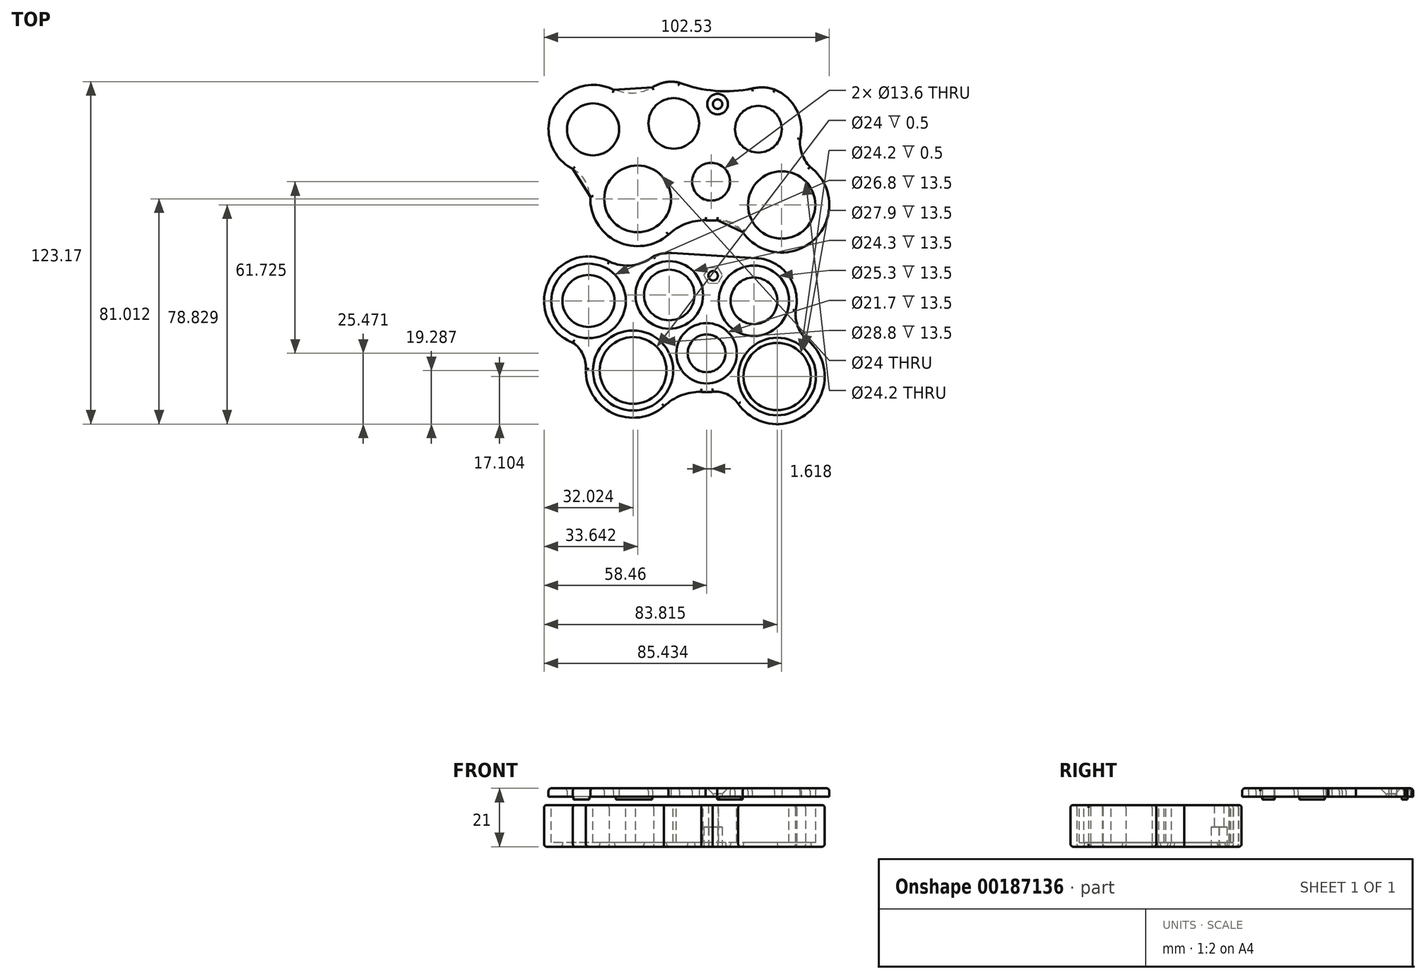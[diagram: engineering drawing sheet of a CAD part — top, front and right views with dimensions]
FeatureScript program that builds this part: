
annotation { "Feature Type Name" : "Feature", "Feature Type Description" : "" }
export const myFeature = defineFeature(function(context is Context, id is Id, definition is map)
    precondition{}
    {
        {
            var Q0;
            Q0=qCreatedBy(makeId("Top.planeOp"),FACE);
            var sketch = newSketch(context, id + "F0", { "sketchPlane" : qUnion([Q0])});
            skArc(sketch, "E0", {"start": v(-18.58, 19.68) * mm, "mid": v(-40.56, 11.98) * mm, "end": v(-31.57, -9.5) * mm});
            skArc(sketch, "E1", {"start": v(2.43, 22.7) * mm, "mid": v(-0.12, 22.37) * mm, "end": v(-2.57, 21.62) * mm});
            skArc(sketch, "E2", {"start": v(48.5, 2.02) * mm, "mid": v(45.84, 14.74) * mm, "end": v(34.4, 20.9) * mm});
            skArc(sketch, "E3", {"start": v(14.55, -27.21) * mm, "mid": v(16.64, -27.35) * mm, "end": v(18.72, -27.17) * mm});
            skArc(sketch, "E4", {"start": v(27.86, -31.53) * mm, "mid": v(53.8, -33.97) * mm, "end": v(52.05, -7.98) * mm});
            skArc(sketch, "E5", {"start": v(-26.9, -18.77) * mm, "mid": v(-17.33, -34.84) * mm, "end": v(1.21, -32.38) * mm});
            skCircle(sketch, "E6", {"center": v(-25.95, 5.48) * mm, "radius": 9.35 * mm});
            skCircle(sketch, "E7", {"center": v(-9.93, -19.53) * mm, "radius": 12 * mm});
            skCircle(sketch, "E8", {"center": v(3.07, 7.61) * mm, "radius": 9.1 * mm});
            skCircle(sketch, "E9", {"center": v(16.51, -13.35) * mm, "radius": 6.8 * mm});
            skCircle(sketch, "E10", {"center": v(33.5, 5.53) * mm, "radius": 8.4 * mm});
            skCircle(sketch, "E11", {"center": v(41.87, -21.72) * mm, "radius": 12.1 * mm});
            skPoint(sketch, "E12", {"position": v(17.46, 2.98) * mm});
            skPoint(sketch, "E13.orphan", {"position": v(18.29, 6.57) * mm});
            skPoint(sketch, "E14.orphan", {"position": v(25, -3.9) * mm});
            skPoint(sketch, "E15.trimOffspring.end.orphan", {"position": v(9.8, -2.87) * mm});
            skPoint(sketch, "E16.center.orphan", {"position": v(16.6, 25.02) * mm});
            skCircle(sketch, "E17", {"center": v(18.84, 14.55) * mm, "radius": 1.7 * mm});
            skArc(sketch, "E18", {"start": v(2.43, 22.7) * mm, "mid": v(3.2, 22.71) * mm, "end": v(3.96, 22.69) * mm});
            skCircle(sketch, "E19", {"center": v(33.5, 5.53) * mm, "radius": 12.5 * mm, "construction": true});
            skCircle(sketch, "E20", {"center": v(3.07, 7.61) * mm, "radius": 12.5 * mm, "construction": true});
            skLineSegment(sketch, "E21", {"start": v(3.07, 7.61) * mm, "end": v(33.5, 5.53) * mm, "construction": true});
            skLineSegment(sketch, "E22", {"start": v(18.29, 6.57) * mm, "end": v(20.04, 32.14) * mm, "construction": true});
            skArc(sketch, "E23", {"start": v(14.82, 17.04) * mm, "mid": v(16.36, 10.53) * mm, "end": v(22.86, 12.08) * mm, "construction": true});
            skLineSegment(sketch, "E24", {"start": v(3.96, 22.69) * mm, "end": v(34.4, 20.9) * mm});
            skArc(sketch, "E25", {"start": v(14.55, -27.21) * mm, "mid": v(7.38, -28.5) * mm, "end": v(1.21, -32.38) * mm});
            skCircle(sketch, "E26", {"center": v(-25.95, 5.48) * mm, "radius": 13.4 * mm, "construction": true});
            skCircle(sketch, "E27", {"center": v(-9.93, -19.53) * mm, "radius": 14.4 * mm, "construction": true});
            skCircle(sketch, "E28", {"center": v(16.51, -13.35) * mm, "radius": 10.85 * mm, "construction": true});
            skCircle(sketch, "E29", {"center": v(3.07, 7.61) * mm, "radius": 12.15 * mm, "construction": true});
            skCircle(sketch, "E30", {"center": v(33.5, 5.53) * mm, "radius": 12.65 * mm, "construction": true});
            skCircle(sketch, "E31", {"center": v(41.87, -21.72) * mm, "radius": 13.95 * mm, "construction": true});
            skArc(sketch, "E32", {"start": v(48.5, 2.02) * mm, "mid": v(49.19, -3.37) * mm, "end": v(52.05, -7.98) * mm});
            skArc(sketch, "E33", {"start": v(-18.58, 19.68) * mm, "mid": v(-12.6, 18.2) * mm, "end": v(-6.52, 19.28) * mm});
            skArc(sketch, "E34", {"start": v(-26.92, -18.94) * mm, "mid": v(-28.02, -13.62) * mm, "end": v(-31.57, -9.5) * mm});
            skArc(sketch, "E35", {"start": v(27.86, -31.53) * mm, "mid": v(23.88, -28.12) * mm, "end": v(18.72, -27.17) * mm});
            skArc(sketch, "E36", {"start": v(-6.52, 19.28) * mm, "mid": v(-4.46, 20.3) * mm, "end": v(-2.57, 21.62) * mm});
            skSolve(sketch);
        }
        {
            var Q0;
            Q0=makeQuery(id+"F0.imprint","IMPRINT",FACE,{"disambiguationData":[TD([[makeQuery(id+"F0.imprint","IMPRINT",EDGE,{"derivedFrom":sQuery(id+"F0.wireOp",EDGE,"E0")}),1.0]])]});
            extrude(context, id + "F1", {"entities" : qUnion([Q0]), "depth" : 15 * mm});
        }
        {
            var Q0;
            Q0=qCreatedBy(makeId("Top.planeOp"),FACE);
            cPlane(context, id + "F2", {"entities" : qUnion([Q0]), "cplaneType" : CPlaneType.OFFSET, "offset" : 18 * mm, "width" : 150 * mm, "height" : 150 * mm});
        }
        {
            var Q0;
            Q0=makeQuery(id+"F1.opExtrude","CAP_FACE",FACE,{"disambiguationData":[OSD([sQuery(id+"F0.wireOp",EDGE,"E0"),sQuery(id+"F0.wireOp",EDGE,"E1"),sQuery(id+"F0.wireOp",EDGE,"E2"),sQuery(id+"F0.wireOp",EDGE,"E3"),sQuery(id+"F0.wireOp",EDGE,"E4"),sQuery(id+"F0.wireOp",EDGE,"E5"),sQuery(id+"F0.wireOp",EDGE,"ujzqgH0S-dhHz-rYZF-uvIy-gRTnRsxaGosE"),sQuery(id+"F0.wireOp",EDGE,"7Unqwi8V-Efat-eiiR-riA2-7JwcXUSN4oi6"),sQuery(id+"F0.wireOp",EDGE,"Qgs0qyWt-UlJd-rMQj-xfdO-Boss06eYTIyV"),sQuery(id+"F0.wireOp",EDGE,"U8kQqLnC-B0kQ-Jbsu-NeVf-h4su2tbWtKO5"),sQuery(id+"F0.wireOp",EDGE,"y7Qm0ll6-VvSp-BIlt-Hxbv-nDPX4vQ1dLlo"),sQuery(id+"F0.wireOp",EDGE,"cmuSQvfR-1LlV-bjM8-RssA-lsbDypLqzE8I"),sQuery(id+"F0.wireOp",EDGE,"E16"),sQuery(id+"F0.wireOp",EDGE,"E6"),sQuery(id+"F0.wireOp",EDGE,"E7"),sQuery(id+"F0.wireOp",EDGE,"E8"),sQuery(id+"F0.wireOp",EDGE,"E9"),sQuery(id+"F0.wireOp",EDGE,"E10"),sQuery(id+"F0.wireOp",EDGE,"E11")])],"isStart":false});
            var sketch = newSketch(context, id + "F3", { "sketchPlane" : qUnion([Q0])});
            skCircle(sketch, "E37", {"center": v(-25.95, 5.48) * mm, "radius": 13.4 * mm});
            skCircle(sketch, "E38", {"center": v(-9.93, -19.53) * mm, "radius": 14.4 * mm});
            skCircle(sketch, "E39", {"center": v(16.51, -13.35) * mm, "radius": 10.85 * mm});
            skCircle(sketch, "E40", {"center": v(3.07, 7.61) * mm, "radius": 12.15 * mm});
            skCircle(sketch, "E41", {"center": v(33.5, 5.53) * mm, "radius": 12.65 * mm});
            skCircle(sketch, "E42", {"center": v(41.87, -21.72) * mm, "radius": 13.95 * mm});
            skSolve(sketch);
        }
        {
            var Q0;
            Q0=makeQuery(id+"F3.imprint","IMPRINT",FACE,{"disambiguationData":[TD([[makeQuery(id+"F3.imprint","IMPRINT",EDGE,{"derivedFrom":sQuery(id+"F3.wireOp",EDGE,"E37")}),1.0]])]});
            var Q1;
            Q1=makeQuery(id+"F3.imprint","IMPRINT",FACE,{"disambiguationData":[TD([[makeQuery(id+"F3.imprint","IMPRINT",EDGE,{"derivedFrom":sQuery(id+"F3.wireOp",EDGE,"E40")}),1.0]])]});
            var Q2;
            Q2=makeQuery(id+"F3.imprint","IMPRINT",FACE,{"disambiguationData":[TD([[makeQuery(id+"F3.imprint","IMPRINT",EDGE,{"derivedFrom":sQuery(id+"F3.wireOp",EDGE,"E41")}),1.0]])]});
            var Q3;
            Q3=makeQuery(id+"F3.imprint","IMPRINT",FACE,{"disambiguationData":[TD([[makeQuery(id+"F3.imprint","IMPRINT",EDGE,{"derivedFrom":sQuery(id+"F3.wireOp",EDGE,"E39")}),1.0]])]});
            var Q4;
            Q4=makeQuery(id+"F3.imprint","IMPRINT",FACE,{"disambiguationData":[TD([[makeQuery(id+"F3.imprint","IMPRINT",EDGE,{"derivedFrom":sQuery(id+"F3.wireOp",EDGE,"E38")}),1.0]])]});
            var Q5;
            Q5=makeQuery(id+"F3.imprint","IMPRINT",FACE,{"disambiguationData":[TD([[makeQuery(id+"F3.imprint","IMPRINT",EDGE,{"derivedFrom":sQuery(id+"F3.wireOp",EDGE,"E42")}),1.0]])]});
            extrude(context, id + "F4", {"entities" : qUnion([Q0, Q1, Q2, Q3, Q4, Q5]), "operationType" : NewBodyOperationType.REMOVE, "oppositeDirection" : true, "depth" : 13.5 * mm});
        }
        {
            var Q0;
            Q0=qCreatedBy(makeId("Top.planeOp"),FACE);
            var sketch = newSketch(context, id + "F5", { "sketchPlane" : qUnion([Q0])});
            skPoint(sketch, "E43", {"position": v(18.84, 14.62) * mm});
            skCircle(sketch, "E44.cCircle", {"center": v(18.84, 14.62) * mm, "radius": 2.86 * mm, "construction": true});
            skLineSegment(sketch, "E44.0", {"start": v(20.44, 17.5) * mm, "end": v(22.14, 14.67) * mm});
            skLineSegment(sketch, "E44.1", {"start": v(22.14, 14.67) * mm, "end": v(20.53, 11.8) * mm});
            skLineSegment(sketch, "E44.2", {"start": v(20.53, 11.8) * mm, "end": v(17.23, 11.74) * mm});
            skLineSegment(sketch, "E44.3", {"start": v(17.23, 11.74) * mm, "end": v(15.54, 14.57) * mm});
            skLineSegment(sketch, "E44.4", {"start": v(15.54, 14.57) * mm, "end": v(17.14, 17.45) * mm});
            skLineSegment(sketch, "E44.5", {"start": v(17.14, 17.45) * mm, "end": v(20.44, 17.5) * mm});
            skPoint(sketch, "E44.0.midPoint", {"position": v(21.29, 16.1) * mm});
            skPoint(sketch, "E45", {"position": v(18.84, 14.55) * mm});
            skSolve(sketch);
        }
        {
            var Q0;
            Q0=makeQuery(id+"F5.imprint","IMPRINT",FACE,{"disambiguationData":[TD([[makeQuery(id+"F5.imprint","IMPRINT",EDGE,{"derivedFrom":sQuery(id+"F5.wireOp",EDGE,"E44.0")}),-1.0]])]});
            extrude(context, id + "F6", {"entities" : qUnion([Q0]), "operationType" : NewBodyOperationType.REMOVE, "depth" : 7 * mm});
        }
        {
            var Q0;
            Q0=qCreatedBy(id+"F2.planeOp",FACE);
            var sketch = newSketch(context, id + "F7", { "sketchPlane" : qUnion([Q0])});
            skArc(sketch, "E46", {"start": v(-16.96, 81.4) * mm, "mid": v(-38.95, 73.7) * mm, "end": v(-29.95, 52.22) * mm});
            skArc(sketch, "E47", {"start": v(1.82, 84.16) * mm, "mid": v(-0.64, 83.47) * mm, "end": v(-2.96, 82.36) * mm});
            skArc(sketch, "E48", {"start": v(50.12, 63.75) * mm, "mid": v(48.8, 74.32) * mm, "end": v(40.94, 81.51) * mm});
            skArc(sketch, "E49", {"start": v(16.17, 34.51) * mm, "mid": v(18.26, 34.38) * mm, "end": v(20.34, 34.55) * mm});
            skArc(sketch, "E50", {"start": v(29.48, 30.2) * mm, "mid": v(55.4, 27.75) * mm, "end": v(53.67, 53.74) * mm});
            skArc(sketch, "E51", {"start": v(-25.3, 42.95) * mm, "mid": v(-15.71, 26.89) * mm, "end": v(2.83, 29.35) * mm});
            skCircle(sketch, "E52", {"center": v(-24.33, 67.2) * mm, "radius": 9.35 * mm});
            skCircle(sketch, "E53", {"center": v(-8.3, 42.2) * mm, "radius": 12 * mm});
            skCircle(sketch, "E54", {"center": v(4.7, 69.34) * mm, "radius": 9.1 * mm});
            skCircle(sketch, "E55", {"center": v(18.13, 48.38) * mm, "radius": 6.8 * mm});
            skCircle(sketch, "E56", {"center": v(35.12, 67.25) * mm, "radius": 8.4 * mm});
            skCircle(sketch, "E57", {"center": v(43.48, 40) * mm, "radius": 12.1 * mm});
            skPoint(sketch, "E58", {"position": v(19.07, 64.7) * mm});
            skPoint(sketch, "E59.orphan", {"position": v(19.9, 68.3) * mm});
            skPoint(sketch, "E60.orphan", {"position": v(26.62, 57.81) * mm});
            skPoint(sketch, "E61.trimOffspring.end.orphan", {"position": v(11.41, 58.86) * mm});
            skPoint(sketch, "E62.center.orphan", {"position": v(18.21, 86.75) * mm});
            skCircle(sketch, "E63", {"center": v(20.45, 76.28) * mm, "radius": 1.7 * mm});
            skCircle(sketch, "E64", {"center": v(35.12, 67.25) * mm, "radius": 12.5 * mm, "construction": true});
            skCircle(sketch, "E65", {"center": v(4.7, 69.34) * mm, "radius": 12.5 * mm, "construction": true});
            skLineSegment(sketch, "E66", {"start": v(4.7, 69.34) * mm, "end": v(35.12, 67.25) * mm, "construction": true});
            skLineSegment(sketch, "E67", {"start": v(19.9, 68.3) * mm, "end": v(21.66, 93.87) * mm, "construction": true});
            skArc(sketch, "E68", {"start": v(16.17, 34.51) * mm, "mid": v(9, 33.23) * mm, "end": v(2.83, 29.35) * mm});
            skCircle(sketch, "E69", {"center": v(-24.33, 67.2) * mm, "radius": 13.4 * mm, "construction": true});
            skCircle(sketch, "E70", {"center": v(-8.3, 42.2) * mm, "radius": 14.4 * mm, "construction": true});
            skCircle(sketch, "E71", {"center": v(18.13, 48.38) * mm, "radius": 10.85 * mm, "construction": true});
            skCircle(sketch, "E72", {"center": v(4.7, 69.34) * mm, "radius": 12.15 * mm, "construction": true});
            skCircle(sketch, "E73", {"center": v(35.12, 67.25) * mm, "radius": 12.65 * mm, "construction": true});
            skCircle(sketch, "E74", {"center": v(43.48, 40) * mm, "radius": 13.95 * mm, "construction": true});
            skArc(sketch, "E75", {"start": v(50.12, 63.75) * mm, "mid": v(50.8, 58.36) * mm, "end": v(53.67, 53.74) * mm});
            skArc(sketch, "E76", {"start": v(-16.96, 81.4) * mm, "mid": v(-10.97, 79.93) * mm, "end": v(-4.9, 81) * mm});
            skArc(sketch, "E77", {"start": v(-25.3, 42.79) * mm, "mid": v(-26.4, 48.1) * mm, "end": v(-29.95, 52.22) * mm});
            skArc(sketch, "E78", {"start": v(29.48, 30.2) * mm, "mid": v(25.5, 33.6) * mm, "end": v(20.34, 34.55) * mm});
            skLineSegment(sketch, "E79", {"start": v(29.48, 30.2) * mm, "end": v(20.34, 34.55) * mm});
            skArc(sketch, "E80", {"start": v(21, 34.23) * mm, "mid": v(25.35, 33.3) * mm, "end": v(28.81, 30.51) * mm});
            skLineSegment(sketch, "E81", {"start": v(-25.3, 42.95) * mm, "end": v(-31.58, 52.94) * mm});
            skArc(sketch, "E82", {"start": v(-25.66, 43.53) * mm, "mid": v(-27.27, 48.9) * mm, "end": v(-31.41, 52.66) * mm});
            skLineSegment(sketch, "E83", {"start": v(-16.96, 81.4) * mm, "end": v(-2.96, 82.36) * mm});
            skArc(sketch, "E84", {"start": v(-16.16, 81.46) * mm, "mid": v(-9.48, 80.34) * mm, "end": v(-3.01, 82.36) * mm});
            skArc(sketch, "E85", {"start": v(-4.9, 81) * mm, "mid": v(-2.84, 82.02) * mm, "end": v(-0.95, 83.34) * mm});
            skArc(sketch, "E86.trimOffspring", {"start": v(23.85, 73) * mm, "mid": v(24.19, 73.39) * mm, "end": v(24.47, 73.8) * mm, "construction": true});
            skCircle(sketch, "E87", {"center": v(20.45, 76.28) * mm, "radius": 4.72 * mm, "construction": true});
            skArc(sketch, "E88", {"start": v(6.7, 83.97) * mm, "mid": v(19.63, 81.07) * mm, "end": v(32.86, 81.87) * mm});
            skArc(sketch, "E89", {"start": v(6.7, 83.97) * mm, "mid": v(4.28, 84.35) * mm, "end": v(1.82, 84.16) * mm});
            skArc(sketch, "E90", {"start": v(40.94, 81.51) * mm, "mid": v(36.93, 82.3) * mm, "end": v(32.86, 81.87) * mm});
            skSolve(sketch);
        }
        {
            var Q0;
            Q0=qSketchRegion(id+"F7",true);
            extrude(context, id + "F8", {"entities" : qUnion([Q0]), "depth" : 3 * mm});
        }
        {
            var Q0;
            Q0=makeQuery(id+"F1.opExtrude","CAP_EDGE",EDGE,{"disambiguationData":[OSD([sQuery(id+"F0.wireOp",EDGE,"E2")])],"isStart":true});
            var Q1;
            Q1=makeQuery(id+"F1.opExtrude","CAP_EDGE",EDGE,{"disambiguationData":[OSD([sQuery(id+"F0.wireOp",EDGE,"cmuSQvfR-1LlV-bjM8-RssA-lsbDypLqzE8I")])],"isStart":true});
            var Q2;
            Q2=makeQuery(id+"F1.opExtrude","CAP_EDGE",EDGE,{"disambiguationData":[OSD([sQuery(id+"F0.wireOp",EDGE,"E1")])],"isStart":true});
            var Q3;
            Q3=makeQuery(id+"F1.opExtrude","CAP_EDGE",EDGE,{"disambiguationData":[OSD([sQuery(id+"F0.wireOp",EDGE,"7Unqwi8V-Efat-eiiR-riA2-7JwcXUSN4oi6")])],"isStart":true});
            var Q4;
            Q4=makeQuery(id+"F1.opExtrude","CAP_EDGE",EDGE,{"disambiguationData":[OSD([sQuery(id+"F0.wireOp",EDGE,"E0")])],"isStart":true});
            var Q5;
            Q5=makeQuery(id+"F1.opExtrude","CAP_EDGE",EDGE,{"disambiguationData":[OSD([sQuery(id+"F0.wireOp",EDGE,"ujzqgH0S-dhHz-rYZF-uvIy-gRTnRsxaGosE")])],"isStart":true});
            var Q6;
            Q6=makeQuery(id+"F1.opExtrude","CAP_EDGE",EDGE,{"disambiguationData":[OSD([sQuery(id+"F0.wireOp",EDGE,"E5")])],"isStart":true});
            var Q7;
            Q7=makeQuery(id+"F1.opExtrude","CAP_EDGE",EDGE,{"disambiguationData":[OSD([sQuery(id+"F0.wireOp",EDGE,"y7Qm0ll6-VvSp-BIlt-Hxbv-nDPX4vQ1dLlo")])],"isStart":true});
            var Q8;
            Q8=makeQuery(id+"F1.opExtrude","CAP_EDGE",EDGE,{"disambiguationData":[OSD([sQuery(id+"F0.wireOp",EDGE,"E3")])],"isStart":true});
            var Q9;
            Q9=makeQuery(id+"F1.opExtrude","CAP_EDGE",EDGE,{"disambiguationData":[OSD([sQuery(id+"F0.wireOp",EDGE,"U8kQqLnC-B0kQ-Jbsu-NeVf-h4su2tbWtKO5")])],"isStart":true});
            var Q10;
            Q10=makeQuery(id+"F1.opExtrude","CAP_EDGE",EDGE,{"disambiguationData":[OSD([sQuery(id+"F0.wireOp",EDGE,"E4")])],"isStart":true});
            var Q11;
            Q11=makeQuery(id+"F1.opExtrude","CAP_EDGE",EDGE,{"disambiguationData":[OSD([sQuery(id+"F0.wireOp",EDGE,"Qgs0qyWt-UlJd-rMQj-xfdO-Boss06eYTIyV")])],"isStart":true});
            var Q12;
            Q12=makeQuery(id+"F1.opExtrude","CAP_EDGE",EDGE,{"disambiguationData":[OSD([sQuery(id+"F0.wireOp",EDGE,"E2")])],"isStart":false});
            var Q13;
            Q13=makeQuery(id+"F1.opExtrude","CAP_EDGE",EDGE,{"disambiguationData":[OSD([sQuery(id+"F0.wireOp",EDGE,"cmuSQvfR-1LlV-bjM8-RssA-lsbDypLqzE8I")])],"isStart":false});
            var Q14;
            Q14=makeQuery(id+"F1.opExtrude","CAP_EDGE",EDGE,{"disambiguationData":[OSD([sQuery(id+"F0.wireOp",EDGE,"E1")])],"isStart":false});
            var Q15;
            Q15=makeQuery(id+"F1.opExtrude","CAP_EDGE",EDGE,{"disambiguationData":[OSD([sQuery(id+"F0.wireOp",EDGE,"7Unqwi8V-Efat-eiiR-riA2-7JwcXUSN4oi6")])],"isStart":false});
            var Q16;
            Q16=makeQuery(id+"F1.opExtrude","CAP_EDGE",EDGE,{"disambiguationData":[OSD([sQuery(id+"F0.wireOp",EDGE,"E0")])],"isStart":false});
            var Q17;
            Q17=makeQuery(id+"F1.opExtrude","CAP_EDGE",EDGE,{"disambiguationData":[OSD([sQuery(id+"F0.wireOp",EDGE,"ujzqgH0S-dhHz-rYZF-uvIy-gRTnRsxaGosE")])],"isStart":false});
            var Q18;
            Q18=makeQuery(id+"F1.opExtrude","CAP_EDGE",EDGE,{"disambiguationData":[OSD([sQuery(id+"F0.wireOp",EDGE,"E5")])],"isStart":false});
            var Q19;
            Q19=makeQuery(id+"F1.opExtrude","CAP_EDGE",EDGE,{"disambiguationData":[OSD([sQuery(id+"F0.wireOp",EDGE,"y7Qm0ll6-VvSp-BIlt-Hxbv-nDPX4vQ1dLlo")])],"isStart":false});
            var Q20;
            Q20=makeQuery(id+"F1.opExtrude","CAP_EDGE",EDGE,{"disambiguationData":[OSD([sQuery(id+"F0.wireOp",EDGE,"E3")])],"isStart":false});
            var Q21;
            Q21=makeQuery(id+"F1.opExtrude","CAP_EDGE",EDGE,{"disambiguationData":[OSD([sQuery(id+"F0.wireOp",EDGE,"U8kQqLnC-B0kQ-Jbsu-NeVf-h4su2tbWtKO5")])],"isStart":false});
            var Q22;
            Q22=makeQuery(id+"F1.opExtrude","CAP_EDGE",EDGE,{"disambiguationData":[OSD([sQuery(id+"F0.wireOp",EDGE,"E4")])],"isStart":false});
            var Q23;
            Q23=makeQuery(id+"F1.opExtrude","CAP_EDGE",EDGE,{"disambiguationData":[OSD([sQuery(id+"F0.wireOp",EDGE,"Qgs0qyWt-UlJd-rMQj-xfdO-Boss06eYTIyV")])],"isStart":false});
            var Q24;
            Q24=makeQuery(id+"F1.opExtrude","CAP_EDGE",EDGE,{"disambiguationData":[OSD([sQuery(id+"F0.wireOp",EDGE,"RsfDVoeq-88MK-O4fM-M0ip-vEhRewOvGteJ")])],"isStart":true});
            var Q25;
            Q25=makeQuery(id+"F1.opExtrude","CAP_EDGE",EDGE,{"disambiguationData":[OSD([sQuery(id+"F0.wireOp",EDGE,"RsfDVoeq-88MK-O4fM-M0ip-vEhRewOvGteJ")])],"isStart":false});
            var Q26;
            Q26=makeQuery(id+"F1.opExtrude","CAP_EDGE",EDGE,{"disambiguationData":[OSD([sQuery(id+"F0.wireOp",EDGE,"cKg1eJ1H-dBtz-pCOY-6ZJL-w3ln1pFaWfeZ")])],"isStart":false});
            var Q27;
            Q27=makeQuery(id+"F1.opExtrude","CAP_EDGE",EDGE,{"disambiguationData":[OSD([sQuery(id+"F0.wireOp",EDGE,"cKg1eJ1H-dBtz-pCOY-6ZJL-w3ln1pFaWfeZ")])],"isStart":true});
            var Q28;
            Q28=makeQuery(id+"F1.opExtrude","CAP_EDGE",EDGE,{"disambiguationData":[OSD([sQuery(id+"F0.wireOp",EDGE,"E8")])],"isStart":true});
            var Q29;
            Q29=makeQuery(id+"F1.opExtrude","CAP_EDGE",EDGE,{"disambiguationData":[OSD([sQuery(id+"F0.wireOp",EDGE,"E10")])],"isStart":true});
            var Q30;
            Q30=makeQuery(id+"F1.opExtrude","CAP_EDGE",EDGE,{"disambiguationData":[OSD([sQuery(id+"F0.wireOp",EDGE,"E11")])],"isStart":true});
            var Q31;
            Q31=makeQuery(id+"F1.opExtrude","CAP_EDGE",EDGE,{"disambiguationData":[OSD([sQuery(id+"F0.wireOp",EDGE,"E9")])],"isStart":true});
            var Q32;
            Q32=makeQuery(id+"F1.opExtrude","CAP_EDGE",EDGE,{"disambiguationData":[OSD([sQuery(id+"F0.wireOp",EDGE,"E7")])],"isStart":true});
            var Q33;
            Q33=makeQuery(id+"F1.opExtrude","CAP_EDGE",EDGE,{"disambiguationData":[OSD([sQuery(id+"F0.wireOp",EDGE,"E6")])],"isStart":true});
            var Q34;
            Q34=makeQuery(id+"F1.opExtrude","CAP_EDGE",EDGE,{"disambiguationData":[OSD([sQuery(id+"F0.wireOp",EDGE,"E18")])],"isStart":false});
            var Q35;
            Q35=makeQuery(id+"F1.opExtrude","CAP_EDGE",EDGE,{"disambiguationData":[OSD([sQuery(id+"F0.wireOp",EDGE,"24nep5WU-dG8d-auV0-GWXn-9hRiig11i69S")])],"isStart":false});
            var Q36;
            Q36=makeQuery(id+"F1.opExtrude","CAP_EDGE",EDGE,{"disambiguationData":[OSD([sQuery(id+"F0.wireOp",EDGE,"ME7NNHAu-M7eQ-ST0F-Oq1P-V6rFcH8f88OT")])],"isStart":false});
            var Q37;
            Q37=makeQuery(id+"F1.opExtrude","CAP_EDGE",EDGE,{"disambiguationData":[OSD([sQuery(id+"F0.wireOp",EDGE,"E18")])],"isStart":true});
            var Q38;
            Q38=makeQuery(id+"F1.opExtrude","CAP_EDGE",EDGE,{"disambiguationData":[OSD([sQuery(id+"F0.wireOp",EDGE,"24nep5WU-dG8d-auV0-GWXn-9hRiig11i69S")])],"isStart":true});
            var Q39;
            Q39=makeQuery(id+"F1.opExtrude","CAP_EDGE",EDGE,{"disambiguationData":[OSD([sQuery(id+"F0.wireOp",EDGE,"ME7NNHAu-M7eQ-ST0F-Oq1P-V6rFcH8f88OT")])],"isStart":true});
            var Q40;
            Q40=makeQuery(id+"F1.opExtrude","CAP_EDGE",EDGE,{"disambiguationData":[OSD([sQuery(id+"F0.wireOp",EDGE,"E25")])],"isStart":false});
            var Q41;
            Q41=makeQuery(id+"F1.opExtrude","CAP_EDGE",EDGE,{"disambiguationData":[OSD([sQuery(id+"F0.wireOp",EDGE,"E35")])],"isStart":false});
            var Q42;
            Q42=makeQuery(id+"F1.opExtrude","CAP_EDGE",EDGE,{"disambiguationData":[OSD([sQuery(id+"F0.wireOp",EDGE,"E32")])],"isStart":false});
            var Q43;
            Q43=makeQuery(id+"F1.opExtrude","CAP_EDGE",EDGE,{"disambiguationData":[OSD([sQuery(id+"F0.wireOp",EDGE,"E34")])],"isStart":false});
            var Q44;
            Q44=makeQuery(id+"F1.opExtrude","CAP_EDGE",EDGE,{"disambiguationData":[OSD([sQuery(id+"F0.wireOp",EDGE,"E33"),sQuery(id+"F0.wireOp",EDGE,"E36")])],"isStart":false});
            var Q45;
            Q45=makeQuery(id+"F1.opExtrude","CAP_EDGE",EDGE,{"disambiguationData":[OSD([sQuery(id+"F0.wireOp",EDGE,"E24")])],"isStart":false});
            var Q46;
            Q46=makeQuery(id+"F1.opExtrude","CAP_EDGE",EDGE,{"disambiguationData":[OSD([sQuery(id+"F0.wireOp",EDGE,"E34")])],"isStart":true});
            var Q47;
            Q47=makeQuery(id+"F1.opExtrude","CAP_EDGE",EDGE,{"disambiguationData":[OSD([sQuery(id+"F0.wireOp",EDGE,"E25")])],"isStart":true});
            var Q48;
            Q48=makeQuery(id+"F1.opExtrude","CAP_EDGE",EDGE,{"disambiguationData":[OSD([sQuery(id+"F0.wireOp",EDGE,"E35")])],"isStart":true});
            var Q49;
            Q49=makeQuery(id+"F1.opExtrude","CAP_EDGE",EDGE,{"disambiguationData":[OSD([sQuery(id+"F0.wireOp",EDGE,"E33"),sQuery(id+"F0.wireOp",EDGE,"E36")])],"isStart":true});
            var Q50;
            Q50=makeQuery(id+"F1.opExtrude","CAP_EDGE",EDGE,{"disambiguationData":[OSD([sQuery(id+"F0.wireOp",EDGE,"E24")])],"isStart":true});
            var Q51;
            Q51=makeQuery(id+"F1.opExtrude","CAP_EDGE",EDGE,{"disambiguationData":[OSD([sQuery(id+"F0.wireOp",EDGE,"E32")])],"isStart":true});
            fillet(context, id + "F9", {"entities" : qUnion([Q0, Q1, Q2, Q3, Q4, Q5, Q6, Q7, Q8, Q9, Q10, Q11, Q12, Q13, Q14, Q15, Q16, Q17, Q18, Q19, Q20, Q21, Q22, Q23, Q24, Q25, Q26, Q27, Q28, Q29, Q30, Q31, Q32, Q33, Q34, Q35, Q36, Q37, Q38, Q39, Q40, Q41, Q42, Q43, Q44, Q45, Q46, Q47, Q48, Q49, Q50, Q51]), "radius" : 1 * mm, "tangentPropagation" : true, "allowEdgeOverflow" : false});
        }
        {
            var Q0;
            Q0=makeQuery(id+"F8.opExtrude","CAP_EDGE",EDGE,{"disambiguationData":[OSD([sQuery(id+"F7.wireOp",EDGE,"dd7925b3-5202-44ba-94b5-5ebd2e67dbee")])],"isStart":false});
            var Q1;
            Q1=makeQuery(id+"F8.opExtrude","CAP_EDGE",EDGE,{"disambiguationData":[OSD([sQuery(id+"F7.wireOp",EDGE,"E48")])],"isStart":false});
            var Q2;
            Q2=makeQuery(id+"F8.opExtrude","CAP_EDGE",EDGE,{"disambiguationData":[OSD([sQuery(id+"F7.wireOp",EDGE,"E75")])],"isStart":false});
            var Q3;
            Q3=makeQuery(id+"F8.opExtrude","CAP_EDGE",EDGE,{"disambiguationData":[OSD([sQuery(id+"F7.wireOp",EDGE,"E47"),sQuery(id+"F7.wireOp",EDGE,"59ef7708-9f98-4fb3-b6a6-863a0492b1ad")])],"isStart":false});
            var Q4;
            Q4=makeQuery(id+"F8.opExtrude","CAP_EDGE",EDGE,{"disambiguationData":[OSD([sQuery(id+"F7.wireOp",EDGE,"E83")])],"isStart":false});
            var Q5;
            Q5=makeQuery(id+"F8.opExtrude","CAP_EDGE",EDGE,{"disambiguationData":[OSD([sQuery(id+"F7.wireOp",EDGE,"E46")])],"isStart":false});
            var Q6;
            Q6=makeQuery(id+"F8.opExtrude","CAP_EDGE",EDGE,{"disambiguationData":[OSD([sQuery(id+"F7.wireOp",EDGE,"E81")])],"isStart":false});
            var Q7;
            Q7=makeQuery(id+"F8.opExtrude","CAP_EDGE",EDGE,{"disambiguationData":[OSD([sQuery(id+"F7.wireOp",EDGE,"E51")])],"isStart":false});
            var Q8;
            Q8=makeQuery(id+"F8.opExtrude","CAP_EDGE",EDGE,{"disambiguationData":[OSD([sQuery(id+"F7.wireOp",EDGE,"E68")])],"isStart":false});
            var Q9;
            Q9=makeQuery(id+"F8.opExtrude","CAP_EDGE",EDGE,{"disambiguationData":[OSD([sQuery(id+"F7.wireOp",EDGE,"E49")])],"isStart":false});
            var Q10;
            Q10=makeQuery(id+"F8.opExtrude","CAP_EDGE",EDGE,{"disambiguationData":[OSD([sQuery(id+"F7.wireOp",EDGE,"E79")])],"isStart":false});
            var Q11;
            Q11=makeQuery(id+"F8.opExtrude","CAP_EDGE",EDGE,{"disambiguationData":[OSD([sQuery(id+"F7.wireOp",EDGE,"E50")])],"isStart":false});
            var Q12;
            Q12=makeQuery(id+"F8.opExtrude","CAP_EDGE",EDGE,{"disambiguationData":[OSD([sQuery(id+"F7.wireOp",EDGE,"E52")])],"isStart":false});
            var Q13;
            Q13=makeQuery(id+"F8.opExtrude","CAP_EDGE",EDGE,{"disambiguationData":[OSD([sQuery(id+"F7.wireOp",EDGE,"E53")])],"isStart":false});
            var Q14;
            Q14=makeQuery(id+"F8.opExtrude","CAP_EDGE",EDGE,{"disambiguationData":[OSD([sQuery(id+"F7.wireOp",EDGE,"E54")])],"isStart":false});
            var Q15;
            Q15=makeQuery(id+"F8.opExtrude","CAP_EDGE",EDGE,{"disambiguationData":[OSD([sQuery(id+"F7.wireOp",EDGE,"E56")])],"isStart":false});
            var Q16;
            Q16=makeQuery(id+"F8.opExtrude","CAP_EDGE",EDGE,{"disambiguationData":[OSD([sQuery(id+"F7.wireOp",EDGE,"E55")])],"isStart":false});
            var Q17;
            Q17=makeQuery(id+"F8.opExtrude","CAP_EDGE",EDGE,{"disambiguationData":[OSD([sQuery(id+"F7.wireOp",EDGE,"E57")])],"isStart":false});
            var Q18;
            Q18=makeQuery(id+"F8.opExtrude","CAP_EDGE",EDGE,{"disambiguationData":[OSD([sQuery(id+"F7.wireOp",EDGE,"E89")])],"isStart":false});
            var Q19;
            Q19=makeQuery(id+"F8.opExtrude","CAP_EDGE",EDGE,{"disambiguationData":[OSD([sQuery(id+"F7.wireOp",EDGE,"E88")])],"isStart":false});
            var Q20;
            Q20=makeQuery(id+"F8.opExtrude","CAP_EDGE",EDGE,{"disambiguationData":[OSD([sQuery(id+"F7.wireOp",EDGE,"E90")])],"isStart":false});
            fillet(context, id + "F10", {"entities" : qUnion([Q0, Q1, Q2, Q3, Q4, Q5, Q6, Q7, Q8, Q9, Q10, Q11, Q12, Q13, Q14, Q15, Q16, Q17, Q18, Q19, Q20]), "radius" : 1 * mm, "tangentPropagation" : true, "allowEdgeOverflow" : false});
        }
        {
            var Q0;
            Q0=makeQuery(id+"F8.opExtrude","CAP_EDGE",EDGE,{"disambiguationData":[OSD([sQuery(id+"F7.wireOp",EDGE,"E63")])],"isStart":false});
            chamfer(context, id + "F11", {"entities" : qUnion([Q0]), "width" : 2 * mm, "tangentPropagation" : true});
        }
        {
            var Q0;
            {var subQ0=sQuery(id+"F7.wireOp",EDGE,"E80");Q0=makeQuery(id+"F7.imprint","IMPRINT",FACE,{"disambiguationData":[TD([[makeQuery(id+"F7.imprint","IMPRINT",EDGE,{"derivedFrom":subQ0}),-1.0]])]});}
            var Q1;
            {var subQ0=sQuery(id+"F7.wireOp",EDGE,"E84");Q1=makeQuery(id+"F7.imprint","IMPRINT",FACE,{"disambiguationData":[TD([[makeQuery(id+"F7.imprint","IMPRINT",EDGE,{"derivedFrom":subQ0}),1.0]])]});}
            var Q2;
            {var subQ0=sQuery(id+"F7.wireOp",EDGE,"E82");Q2=makeQuery(id+"F7.imprint","IMPRINT",FACE,{"disambiguationData":[TD([[makeQuery(id+"F7.imprint","IMPRINT",EDGE,{"derivedFrom":subQ0}),1.0]])]});}
            extrude(context, id + "F12", {"entities" : qUnion([Q0, Q1, Q2]), "operationType" : NewBodyOperationType.ADD, "oppositeDirection" : true, "depth" : 1 * mm});
        }
    });
